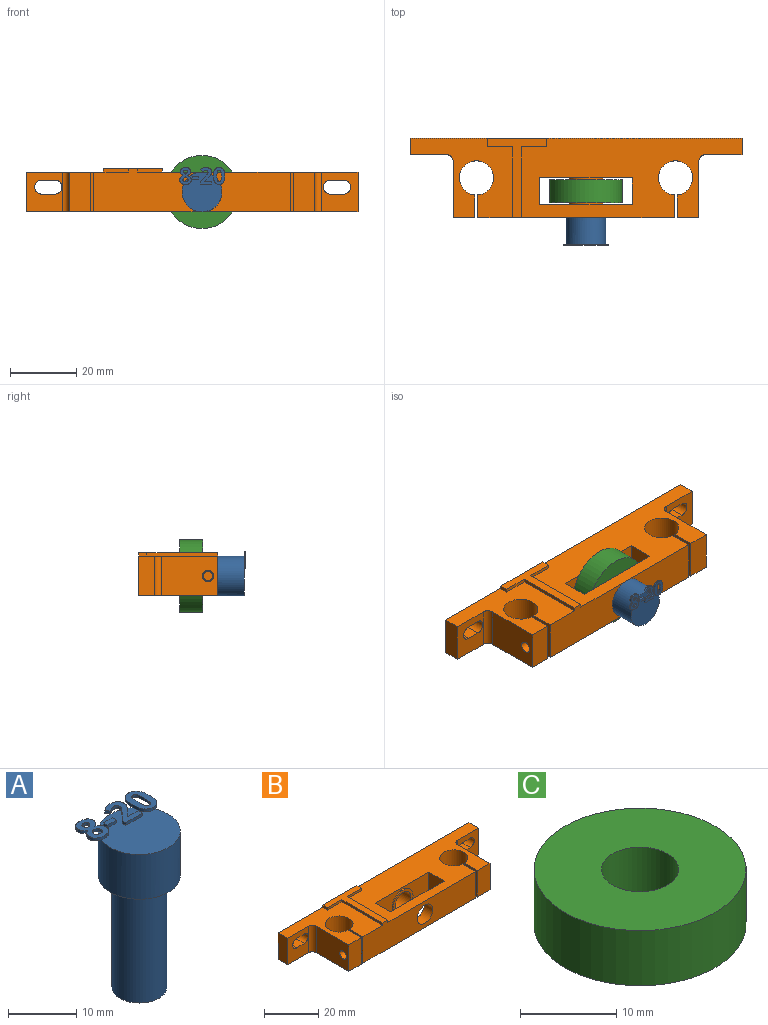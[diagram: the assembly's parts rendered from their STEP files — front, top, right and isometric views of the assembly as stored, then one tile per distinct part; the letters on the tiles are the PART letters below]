
ASSEMBLY  parts=3 mates=2
PART A: 89 faces, bbox 13.6x13.4x28.5 mm
  f0: plane 0.75x0.57mm, normal (0,0,1), area 0.1mm2, adj f5,f78,f79
  f1: plane 12x12mm, normal (0,0,1), area 100.3mm2, adj f5,f22,f23,f24,f25,f26,f40,f41
  f2: plane 1.04x0.97mm, normal (0,0,1), area 0.5mm2, adj f5,f29,f30,f31,f32,f33
  f3: cylinder r=4mm len=20mm, axis (0,0,-1), area 502.7mm2, adj f4,f6
  f4: plane 8x8mm, normal (0,0,-1), area 50.3mm2, adj f3
  f5: cylinder r=6mm len=12mm, axis (0,0,-1), area 301.6mm2, adj f0,f1,f2,f6,f39,f70,f88
  f6: plane 12x12mm, normal (0,0,-1), area 62.8mm2, adj f3,f5
  f7: extruded ~0.5x0.43mm, area 0.2mm2, adj f8,f37,f38,f39
  f8: extruded ~0.5x0.43mm, area 0.2mm2, adj f7,f9,f38,f39
  f9: extruded ~0.5x0.37mm, area 0.2mm2, adj f8,f10,f38,f39
  f10: extruded ~0.5x0.38mm, area 0.2mm2, adj f9,f11,f38,f39
  f11: extruded ~0.5x0.46mm, area 0.3mm2, adj f10,f12,f38,f39
  f12: extruded ~0.5x0.47mm, area 0.3mm2, adj f11,f13,f38,f39
  f13: extruded ~0.5x0.36mm, area 0.2mm2, adj f12,f37,f38,f39
  f14: extruded ~1.15x0.5mm, area 0.6mm2, adj f15,f35,f38,f39
  f15: extruded ~1.15x0.5mm, area 0.6mm2, adj f14,f16,f38,f39
  f16: extruded ~0.86x0.5mm, area 0.5mm2, adj f15,f17,f38,f39
  f17: extruded ~0.67x0.5mm, area 0.4mm2, adj f16,f18,f38,f39
  f18: extruded ~0.61x0.57mm, area 0.4mm2, adj f17,f19,f38,f39
  f19: extruded ~0.72x0.58mm, area 0.5mm2, adj f18,f20,f38,f39
  f20: extruded ~0.75x0.5mm, area 0.4mm2, adj f19,f21,f38,f39
  f21: extruded ~0.98x0.5mm, area 0.6mm2, adj f20,f22,f38,f39
  f22: extruded ~1.28x0.5mm, area 0.7mm2, adj f1,f21,f23,f38,f39
  f23: extruded ~1.26x0.5mm, area 0.7mm2, adj f1,f22,f24,f38
  f24: extruded ~0.98x0.5mm, area 0.6mm2, adj f1,f23,f25,f38
  f25: extruded ~0.71x0.5mm, area 0.4mm2, adj f1,f24,f26,f38
  f26: extruded ~0.8x0.62mm, area 0.5mm2, adj f1,f25,f27,f38,f39
  f27: extruded ~0.68x0.53mm, area 0.4mm2, adj f26,f28,f38,f39
  f28: extruded ~0.68x0.5mm, area 0.4mm2, adj f27,f35,f38,f39
  f29: extruded ~0.62x0.5mm, area 0.4mm2, adj f2,f30,f36,f38,f39
  f30: extruded ~0.5x0.43mm, area 0.2mm2, adj f2,f29,f31,f38
  f31: extruded ~0.5x0.44mm, area 0.2mm2, adj f2,f30,f32,f38
  f32: extruded ~0.58x0.5mm, area 0.3mm2, adj f2,f31,f33,f38
  f33: extruded ~0.56x0.5mm, area 0.3mm2, adj f2,f32,f34,f38,f39
  f34: extruded ~0.5x0.45mm, area 0.3mm2, adj f33,f36,f38,f39
  f35: extruded ~0.87x0.5mm, area 0.5mm2, adj f14,f28,f38,f39
  f36: extruded ~0.84x0.72mm, area 0.6mm2, adj f29,f34,f38,f39
  f37: extruded ~0.5x0.37mm, area 0.2mm2, adj f7,f13,f38,f39
  f38: plane 5.09x3.48mm, normal (0,0,1), area 11.2mm2, adj f7,f8,f9,f10,f11,f12,f13,f14
  f39: plane 5.05x3.32mm, normal (0,0,-1), area 8.6mm2, adj f5,f7,f8,f9,f10,f11,f12,f13
  f40: plane 0.85x0.5mm, normal (-1,0,0), area 0.4mm2, adj f1,f41,f43,f44
  f41: plane 1.82x0.5mm, normal (0,-1,0), area 0.9mm2, adj f1,f40,f42,f44
  f42: plane 0.85x0.5mm, normal (1,0,0), area 0.4mm2, adj f1,f41,f43,f44
  f43: plane 1.82x0.5mm, normal (0,1,0), area 0.9mm2, adj f1,f40,f42,f44
  f44: plane 1.82x0.85mm, normal (0,0,1), area 1.5mm2, adj f40,f41,f42,f43
  f45: extruded ~0.5x0.39mm, area 0.2mm2, adj f1,f46,f68,f69,f70
  f46: extruded ~0.5x0.41mm, area 0.2mm2, adj f1,f45,f47,f69
  f47: extruded ~0.78x0.72mm, area 0.5mm2, adj f1,f46,f48,f69
  f48: plane 1.26x1.24mm, normal (-0.71,0.7,0), area 0.9mm2, adj f1,f47,f49,f69
  f49: plane 0.73x0.5mm, normal (-1,0,0), area 0.4mm2, adj f1,f48,f50,f69
  f50: plane 3.46x0.5mm, normal (0,-1,0), area 1.7mm2, adj f1,f49,f51,f69
  f51: plane 0.88x0.5mm, normal (1,0,0), area 0.4mm2, adj f1,f50,f52,f69
  f52: plane 2.16x0.5mm, normal (0,1,0), area 1.1mm2, adj f1,f51,f53,f69
  f53: plane 0.5x0.05mm, normal (1,0,0), area 0mm2, adj f1,f52,f54,f69
  f54: plane 0.64x0.6mm, normal (0.69,-0.73,0), area 0.4mm2, adj f1,f53,f55,f69
  f55: extruded ~0.9x0.89mm, area 0.6mm2, adj f1,f54,f56,f69
  f56: extruded ~0.62x0.5mm, area 0.4mm2, adj f1,f55,f57,f69,f70
  f57: extruded ~0.64x0.5mm, area 0.3mm2, adj f56,f58,f69,f70
  f58: extruded ~0.7x0.5mm, area 0.4mm2, adj f57,f59,f69,f70
  f59: extruded ~0.55x0.5mm, area 0.4mm2, adj f58,f60,f69,f70
  f60: extruded ~0.82x0.5mm, area 0.4mm2, adj f59,f61,f69,f70
  f61: extruded ~0.64x0.5mm, area 0.3mm2, adj f60,f62,f69,f70
  f62: extruded ~0.53x0.5mm, area 0.3mm2, adj f61,f63,f69,f70
  f63: extruded ~0.61x0.5mm, area 0.4mm2, adj f62,f64,f69,f70
  f64: plane 0.67x0.57mm, normal (-0.76,-0.65,0), area 0.4mm2, adj f63,f65,f69,f70
  f65: extruded ~0.57x0.5mm, area 0.3mm2, adj f64,f66,f69,f70
  f66: extruded ~0.56x0.5mm, area 0.3mm2, adj f65,f67,f69,f70
  f67: extruded ~0.5x0.44mm, area 0.2mm2, adj f66,f68,f69,f70
  f68: extruded ~0.5x0.44mm, area 0.2mm2, adj f45,f67,f69,f70
  f69: plane 5.03x3.48mm, normal (0,0,1), area 9.1mm2, adj f45,f46,f47,f48,f49,f50,f51,f52
  f70: plane 3.34x2.04mm, normal (0,0,-1), area 3.5mm2, adj f5,f45,f56,f57,f58,f59,f60,f61
  f71: extruded ~1.92x0.5mm, area 1mm2, adj f72,f86,f87,f88
  f72: extruded ~1.91x0.5mm, area 1mm2, adj f71,f73,f87,f88
  f73: extruded ~1.3x0.65mm, area 0.8mm2, adj f72,f74,f87,f88
  f74: extruded ~1.3x0.62mm, area 0.8mm2, adj f73,f75,f87,f88
  f75: extruded ~1.93x0.5mm, area 1mm2, adj f1,f74,f76,f87,f88
  f76: extruded ~1.9x0.5mm, area 1mm2, adj f1,f75,f77,f87
  f77: extruded ~1.29x0.64mm, area 0.8mm2, adj f1,f76,f86,f87
  f78: extruded ~0.53x0.5mm, area 0.4mm2, adj f0,f79,f85,f87,f88
  f79: extruded ~1.31x0.5mm, area 0.7mm2, adj f0,f78,f80,f87,f88
  f80: extruded ~1.31x0.5mm, area 0.7mm2, adj f79,f81,f87,f88
  f81: extruded ~0.53x0.5mm, area 0.4mm2, adj f80,f82,f87,f88
  f82: extruded ~0.53x0.5mm, area 0.4mm2, adj f81,f83,f87,f88
  f83: extruded ~1.31x0.5mm, area 0.7mm2, adj f82,f84,f87,f88
  f84: extruded ~1.3x0.5mm, area 0.7mm2, adj f83,f85,f87,f88
  f85: extruded ~0.53x0.5mm, area 0.4mm2, adj f78,f84,f87,f88
  f86: extruded ~1.31x0.62mm, area 0.8mm2, adj f1,f71,f77,f87,f88
  f87: plane 5.1x3.46mm, normal (0,0,1), area 10.7mm2, adj f71,f72,f73,f74,f75,f76,f77,f78
  f88: plane 5.1x3.46mm, normal (0,0,-1), area 8.4mm2, adj f5,f71,f72,f73,f74,f75,f78,f79
PART B: 53 faces, bbox 100x24x13 mm
  f0: plane 100x24mm, normal (0,0,1), area 1402.2mm2, adj f2,f3,f4,f5,f6,f7,f8,f9
  f1: plane 100x24mm, normal (0,0,-1), area 1505.1mm2, adj f2,f3,f4,f5,f6,f7,f8,f9
  f2: plane 100x12mm, normal (0,1,0), area 1138.7mm2, adj f0,f1,f6,f11,f18,f19,f20,f21
  f3: plane 12x11mm, normal (0,-1,0), area 101.3mm2, adj f0,f1,f11,f22,f23,f24,f25,f48
  f4: plane 12x6.56mm, normal (0,-1,0), area 78.7mm2, adj f0,f1,f10,f16
  f5: plane 59.12x13mm, normal (0,-1,0), area 659.4mm2, adj f0,f1,f14,f17,f26,f37,f38,f44
  f6: plane 12x5mm, normal (-1,0,0), area 60mm2, adj f0,f1,f2,f7
  f7: plane 12x11mm, normal (0,-1,0), area 101.3mm2, adj f0,f1,f6,f18,f19,f20,f21,f52
  f8: plane 17x12mm, normal (-1,0,0), area 194.9mm2, adj f0,f1,f9,f51,f52
  f9: plane 12x6.56mm, normal (0,-1,0), area 78.7mm2, adj f0,f1,f8,f13
  f10: plane 17x12mm, normal (1,0,0), area 194.9mm2, adj f0,f1,f4,f47,f48
  f11: plane 12x5mm, normal (1,0,0), area 60mm2, adj f0,f1,f2,f3
  f12: cylinder r=5.15mm len=12mm, axis (0,0,1), area 377.8mm2, adj f0,f1,f13,f14
  f13: plane 12x6.87mm, normal (1,0,0), area 73.3mm2, adj f0,f1,f9,f12,f51
  f14: plane 12x6.87mm, normal (-1,0,0), area 76.3mm2, adj f0,f1,f5,f12,f50
  f15: cylinder r=5.15mm len=12mm, axis (0,0,1), area 377.8mm2, adj f0,f1,f16,f17
  f16: plane 12x6.87mm, normal (-1,0,0), area 73.3mm2, adj f0,f1,f4,f15,f47
  f17: plane 12x6.87mm, normal (1,0,0), area 76.3mm2, adj f0,f1,f5,f15,f46
  f18: cylinder r=2.1mm len=5mm, axis (0,1,0), area 33mm2, adj f2,f7,f19,f21
  f19: plane 5x4mm, normal (0,0,1), area 20mm2, adj f2,f7,f18,f20
  f20: cylinder r=2.1mm len=5mm, axis (0,1,0), area 33mm2, adj f2,f7,f19,f21
  f21: plane 5x4mm, normal (0,0,-1), area 20mm2, adj f2,f7,f18,f20
  f22: plane 5x4mm, normal (0,0,-1), area 20mm2, adj f2,f3,f23,f25
  f23: cylinder r=2.1mm len=5mm, axis (0,1,0), area 33mm2, adj f2,f3,f22,f24
  f24: plane 5x4mm, normal (0,0,1), area 20mm2, adj f2,f3,f23,f25
  f25: cylinder r=2.1mm len=5mm, axis (0,1,0), area 33mm2, adj f2,f3,f22,f24
  f26: cylinder r=4.1mm len=8.2mm, axis (0,-1,0), area 115.9mm2, adj f5,f36
  f27: plane 12x8mm, normal (1,0,0), area 96mm2, adj f0,f1,f29,f30
  f28: plane 12x8mm, normal (-1,0,0), area 96mm2, adj f0,f1,f29,f30
  f29: plane 28x12mm, normal (0,-1,0), area 251.2mm2, adj f0,f1,f27,f28,f31
  f30: plane 28x12mm, normal (0,1,0), area 249.3mm2, adj f0,f1,f27,f28,f35
  f31: cylinder r=5.2mm len=10.39mm, axis (0,1,0), area 16.3mm2, adj f29,f32
  f32: plane 10.39x10.39mm, normal (0,-1,0), area 32mm2, adj f31,f34
  f33: plane 8.2x8.2mm, normal (0,-1,0), area 52.8mm2, adj f34
  f34: cylinder r=4.1mm len=8.5mm, axis (0,-1,0), area 219mm2, adj f32,f33
  f35: cylinder r=5.25mm len=10.51mm, axis (0,-1,0), area 16.5mm2, adj f30,f36
  f36: plane 10.51x10.51mm, normal (0,1,0), area 33.9mm2, adj f26,f35
  f37: plane 21.34x1mm, normal (-1,0,0), area 21.3mm2, adj f0,f5,f43,f44
  f38: plane 21.34x1mm, normal (1,0,0), area 21.3mm2, adj f0,f5,f39,f44
  f39: plane 7.54x1mm, normal (0,-1,0), area 7.5mm2, adj f0,f38,f40,f44
  f40: plane 2.46x1mm, normal (1,0,0), area 2.5mm2, adj f0,f39,f41,f44
  f41: plane 17.84x1mm, normal (0,1,0), area 17.8mm2, adj f0,f40,f42,f44
  f42: plane 2.46x1mm, normal (-1,0,0), area 2.5mm2, adj f0,f41,f43,f44
  f43: plane 7.54x1mm, normal (0,-1,0), area 7.5mm2, adj f0,f37,f42,f44
  f44: plane 23.8x17.84mm, normal (0,0,1), area 102.9mm2, adj f5,f37,f38,f39,f40,f41,f42,f43
  f45: plane 2.8x2.8mm, normal (1,0,0), area 6.2mm2, adj f46
  f46: cylinder r=1.4mm len=10.56mm, axis (1,0,0), area 92.9mm2, adj f17,f45
  f47: cylinder r=1.7mm len=6.56mm, axis (1,0,0), area 70.1mm2, adj f10,f16
  f48: cylinder r=2mm len=12mm, axis (0,0,1), area 37.7mm2, adj f0,f1,f3,f10
  f49: plane 2.8x2.8mm, normal (-1,0,0), area 6.2mm2, adj f50
  f50: cylinder r=1.4mm len=10.56mm, axis (-1,0,0), area 92.9mm2, adj f14,f49
  f51: cylinder r=1.7mm len=6.56mm, axis (-1,0,0), area 70.1mm2, adj f8,f13
  f52: cylinder r=2mm len=12mm, axis (0,0,1), area 37.7mm2, adj f0,f1,f7,f8
PART C: 4 faces, bbox 22x22x7 mm
  f0: cylinder r=4mm len=8mm, axis (0,0,-1), area 175.9mm2, adj f2,f3
  f1: cylinder r=11mm len=22mm, axis (0,0,-1), area 483.8mm2, adj f2,f3
  f2: plane 22x22mm, normal (0,0,1), area 329.9mm2, adj f0,f1
  f3: plane 22x22mm, normal (0,0,-1), area 329.9mm2, adj f0,f1
PLACE A rot(axis=(1,0,0),90deg) t=(5.95,13.74,6.05)mm
PLACE B t=(-0.7,5.43,0.05)mm
PLACE C rot(axis=(-1,0,0),90deg) t=(5.95,-1.76,6.05)mm
MATE fastened C.f0 <-> B.f26  axis (0,1,0) through (5.95,5.24,6.05)mm
MATE fastened A.f3 <-> B.f26  axis (0,1,0) through (5.95,-6.26,6.05)mm
